FCSTD DOCUMENT  (FreeCAD 1.2R20260113 (Git shallow))
Label: Chaine verouillable
License: Creative Commons Attribution-NonCommercial-ShareAlike 4.0
LicenseURL: https://creativecommons.org/licenses/by-nc-sa/4.0/
objects: Sketcher::SketchObject×15, App::Point×12, PartDesign::Pocket×10, PartDesign::Body×9, PartDesign::SubShapeBinder×6, PartDesign::Pad×6, PartDesign::Mirrored×5, Part::FeaturePython×4, PartDesign::Draft×3, PartDesign::Chamfer×3, App::Part×3, PartDesign::FeatureBase×2, PartDesign::FeaturePython×2, PartDesign::Thickness×1, App::VarSet×1, Part::DatumLine×1, PartDesign::Hole×1, PartDesign::Groove×1
note: 142 computed .brp shape members not serialized (recipe doc carries the construction recipe); baked Part::Feature solids carry a one-line shape summary decoded from their .brp

FEATURE [App::Point] Origin001  label="Origine"
  Role = Origin
FEATURE [Sketcher::SketchObject] Sketch  label="Master"
  ArcFitTolerance = 1e-06
  AttachmentSupport = -> [Origin]
  ExternalTypes = [0]
  FullyConstrained = true
  MakeInternals = false
  MapMode = 5
  sketch-geometry (8):
    g0: ArcOfCircle CenterX=0 CenterY=1.93649 CenterZ=0 NormalX=0 NormalY=0 NormalZ=1 AngleXU=0 Radius=4 StartAngle=5.77782 EndAngle=9.93014
    g1: ArcOfCircle CenterX=7 CenterY=-1.93649 CenterZ=0 NormalX=0 NormalY=0 NormalZ=1 AngleXU=0 Radius=4 StartAngle=2.63623 EndAngle=4.71239
    g2: ArcOfCircle CenterX=-7 CenterY=-1.93649 CenterZ=0 NormalX=0 NormalY=0 NormalZ=1 AngleXU=0 Radius=4 StartAngle=4.71239 EndAngle=6.78855
    g3: LineSegment StartX=-7 StartY=-5.93649 StartZ=0 EndX=-7 EndY=-9.93649 EndZ=0
    g4: LineSegment StartX=-7 StartY=-9.93649 StartZ=0 EndX=7 EndY=-9.93649 EndZ=0
    g5: LineSegment StartX=7 StartY=-9.93649 StartZ=0 EndX=7 EndY=-5.93649 EndZ=0
    g6: LineSegment [constr] StartX=0 StartY=1.93649 StartZ=0 EndX=0 EndY=0 EndZ=0
    g7: LineSegment [constr] StartX=7 StartY=-1.93649 StartZ=0 EndX=7 EndY=0 EndZ=0
  constraints (23):
    c: Symmetric(g2,g1,g-2)
    c: Tangent(g2,g0) = 1.5708
    c: Tangent(g1,g0) = 1.5708
    c: Equal(g1,g0)
    c: Radius(g0) = 4
    c: Coincident(g2,g3)
    c: Coincident(g3,g4)
    c: Horizontal(g4)
    c: Coincident(g4,g5)
    c: Coincident(g5,g1)
    c: Vertical(g5)
    c: Vertical(g1,g1)
    c: Vertical(g2,g2)
    c: Vertical(g3)
    c: Distance(g5,g5) = 4
    c: PointOnObject(g0,g-2)
    c: Coincident(g6,g0)
    c: Coincident(g6,g-1)
    c: Coincident(g7,g1)
    c: PointOnObject(g7,g-1)
    c: Vertical(g7)
    c: Equal(g7,g6)
    c: Distance(g4,g4) = 14
FEATURE [App::Point] Origin003  label="Origine002"
  Role = Origin
FEATURE [PartDesign::SubShapeBinder] Binder
  BindCopyOnChange = 0
  BindMode = 0
  ClaimChildren = false
  Context = -> Body001 [Binder.]
  Fuse = false
  MakeFace = true
  OffsetFill = false
  OffsetIntersection = false
  OffsetJoinType = 0
  OffsetOpenResult = false
  PartialLoad = false
  Refine = true
  Relative = true
  Support = -> [Body[Sketch.]]
  _Version = 2
FEATURE [PartDesign::Pad] Pad
  Direction = (0,0,1)
  Length = 10
  Length2 = 10
  Profile = -> Binder [Face1]
  Refine = true
  SideType = 0
  Suppressed = false
  Type = 0
  Type2 = 0
FEATURE [PartDesign::Draft] Draft
  Angle = -10
  Base = -> Pad [Face6,Face1,Face2]
  BaseFeature = -> Pad
  Refine = true
  SupportTransform = false
  Suppressed = false
FEATURE [PartDesign::Mirrored] Mirrored
  BaseFeature = -> Draft
  MirrorPlane = -> XY_Plane001
  Originals = -> [Draft]
  Refine = true
  Suppressed = false
  TransformMode = 1
FEATURE [PartDesign::Body] Body001  label="v1 Male"
  AllowCompound = false
  Group = -> [Binder,Pad,Draft,Mirrored]
  Origin = -> Origin002
  Tip = -> Mirrored
FEATURE [App::Point] Origin005  label="Origine004"
  Role = Origin
FEATURE [Sketcher::SketchObject] Sketch001
  ArcFitTolerance = 1e-06
  AttachmentSupport = -> [Origin]
  ExternalGeometry = -> [Sketch]
  ExternalTypes = [0,0]
  FullyConstrained = true
  MakeInternals = false
  MapMode = 5
  sketch-geometry (6):
    g0: ArcOfCircle CenterX=7 CenterY=-1.93649 CenterZ=0 NormalX=0 NormalY=0 NormalZ=1 AngleXU=0 Radius=4 StartAngle=2.63623 EndAngle=6.78855
    g1: ArcOfCircle CenterX=0 CenterY=1.93649 CenterZ=0 NormalX=0 NormalY=0 NormalZ=1 AngleXU=0 Radius=4 StartAngle=5.77782 EndAngle=7.85398
    g2: ArcOfCircle CenterX=14 CenterY=1.93649 CenterZ=0 NormalX=0 NormalY=0 NormalZ=1 AngleXU=0 Radius=4 StartAngle=1.5708 EndAngle=3.64695
    g3: LineSegment StartX=1.2e-15 StartY=5.93649 StartZ=0 EndX=1.2e-15 EndY=7.93649 EndZ=0
    g4: LineSegment StartX=1.2e-15 StartY=7.93649 StartZ=0 EndX=14 EndY=7.93649 EndZ=0
    g5: LineSegment StartX=14 StartY=7.93649 StartZ=0 EndX=14 EndY=5.93649 EndZ=0
  constraints (18):
    c: Coincident(g0,g-3)
    c: Coincident(g0,g-4)
    c: PointOnObject(g0,g-1)
    c: Coincident(g1,g-4)
    c: Coincident(g1,g0)
    c: Coincident(g2,g0)
    c: Coincident(g1,g3)
    c: Coincident(g3,g4)
    c: Horizontal(g4)
    c: Coincident(g4,g5)
    c: Coincident(g5,g2)
    c: Vertical(g5)
    c: Equal(g2,g1)
    c: Horizontal(g2,g1)
    c: Vertical(g3)
    c: Distance(g5,g5) = 2
    c: Vertical(g2,g2)
    c: Vertical(g1,g-1)
FEATURE [PartDesign::Body] Body
  AllowCompound = false
  Group = -> [Sketch,Sketch001]
  Origin = -> Origin
FEATURE [PartDesign::SubShapeBinder] Binder001
  BindCopyOnChange = 0
  BindMode = 0
  ClaimChildren = false
  Context = -> Body002 [Binder001.]
  Fuse = false
  MakeFace = true
  OffsetFill = false
  OffsetIntersection = false
  OffsetJoinType = 0
  OffsetOpenResult = false
  PartialLoad = false
  Refine = true
  Relative = true
  Support = -> [Body[Sketch001.]]
  _Version = 2
FEATURE [PartDesign::Pad] Pad001
  Direction = (0,0,1)
  Length = 10
  Length2 = 10
  Profile = -> Binder001
  Refine = true
  SideType = 0
  Suppressed = false
  Type = 0
  Type2 = 0
FEATURE [PartDesign::Draft] Draft001
  Angle = 10
  Base = -> Pad001 [Face6,Face1,Face2]
  BaseFeature = -> Pad001
  Refine = true
  SupportTransform = false
  Suppressed = false
FEATURE [PartDesign::Thickness] Thickness
  Base = -> Draft001 [Face8]
  BaseFeature = -> Draft001
  Intersection = true
  Join = 0
  Mode = 0
  Refine = true
  Reversed = true
  SupportTransform = false
  Suppressed = false
  Value = 2
FEATURE [PartDesign::Mirrored] Mirrored001
  BaseFeature = -> Thickness
  MirrorPlane = -> XY_Plane002
  Originals = -> [Draft001]
  Refine = true
  Suppressed = false
  TransformMode = 1
FEATURE [PartDesign::Body] Body002  label="v1 Female"
  AllowCompound = false
  Group = -> [Binder001,Pad001,Draft001,Thickness,Mirrored001]
  Origin = -> Origin004
  Placement = pos=(-7,0,0) rot=(0,0,1;3.14159rad)
  Tip = -> Mirrored001
FEATURE [App::Point] Origin007  label="Origine006"
  Role = Origin
FEATURE [Sketcher::SketchObject] Sketch002
  ArcFitTolerance = 1e-06
  AttachmentSupport = -> [Origin006]
  ExternalTypes = [0]
  FullyConstrained = true
  MakeInternals = false
  MapMode = 5
  sketch-geometry (13):
    g0: LineSegment StartX=-10 StartY=10 StartZ=0 EndX=-10 EndY=-10 EndZ=0
    g1: LineSegment StartX=-10 StartY=-10 StartZ=0 EndX=-8 EndY=-10 EndZ=0
    g2: LineSegment StartX=-8 StartY=-10 StartZ=0 EndX=-8 EndY=0 EndZ=0
    g3: LineSegment StartX=-8 StartY=0 StartZ=0 EndX=8 EndY=0 EndZ=0
    g4: LineSegment StartX=8 StartY=0 StartZ=0 EndX=8 EndY=-10 EndZ=0
    g5: LineSegment StartX=8 StartY=-10 StartZ=0 EndX=10 EndY=-10 EndZ=0
    g6: LineSegment StartX=10 StartY=-10 StartZ=0 EndX=10 EndY=10 EndZ=0
    g7: LineSegment StartX=10 StartY=10 StartZ=0 EndX=8 EndY=10 EndZ=0
    g8: LineSegment StartX=8 StartY=10 StartZ=0 EndX=8 EndY=2 EndZ=0
    g9: LineSegment StartX=8 StartY=2 StartZ=0 EndX=-8 EndY=2 EndZ=0
    g10: LineSegment StartX=-8 StartY=2 StartZ=0 EndX=-8 EndY=10 EndZ=0
    g11: LineSegment StartX=-8 StartY=10 StartZ=0 EndX=-10 EndY=10 EndZ=0
    g12: LineSegment [constr] StartX=-8 StartY=2 StartZ=0 EndX=-8 EndY=0 EndZ=0
  constraints (36):
    c: Coincident(g0,g1)
    c: Coincident(g1,g2)
    c: PointOnObject(g2,g-1)
    c: Vertical(g2)
    c: Coincident(g2,g3)
    c: PointOnObject(g3,g-1)
    c: Coincident(g3,g4)
    c: Vertical(g4)
    c: Coincident(g4,g5)
    c: Horizontal(g5)
    c: Coincident(g5,g6)
    c: Vertical(g6)
    c: Coincident(g6,g7)
    c: Horizontal(g7)
    c: Coincident(g7,g8)
    c: Coincident(g8,g9)
    c: Horizontal(g9)
    c: Coincident(g9,g10)
    c: Vertical(g10)
    c: Coincident(g10,g11)
    c: Coincident(g11,g0)
    c: Horizontal(g11)
    c: Vertical(g8)
    c: Coincident(g12,g9)
    c: Coincident(g12,g2)
    c: Vertical(g12)
    c: Equal(g12,g11)
    c: Equal(g11,g7)
    c: Distance(g11,g11) = 2
    c: DistanceY(g0,g0) = 20
    c: Horizontal(g1)
    c: DistanceX(g0,g5) = 20
    c: Symmetric(g1,g4,g-2)
    c: Symmetric(g0,g0,g-1)
    c: Horizontal(g10,g7)
    c: Vertical(g3,g8)
FEATURE [PartDesign::Pad] Pad002
  Direction = (0,0,1)
  Length = 18.8496
  Length2 = 10
  Profile = -> Sketch002
  ReferenceAxis = -> Sketch002 [N_Axis]
  Refine = true
  SideType = 2
  Suppressed = false
  Type = 0
  Type2 = 0
  expr: Length = 6 * pi
FEATURE [Sketcher::SketchObject] Sketch003
  ArcFitTolerance = 1e-06
  ExternalGeometry = -> [Pad002]
  ExternalTypes = [0,0]
  FullyConstrained = true
  MakeInternals = false
  MapMode = 5
  Placement = pos=(8,0,0) rot=(0.57735,-0.57735,-0.57735;2.0944rad)
  sketch-geometry (10):
    g0: LineSegment StartX=-10 StartY=13.4248 StartZ=0 EndX=-10 EndY=4.42478 EndZ=0
    g1: LineSegment StartX=-10 StartY=4.42478 StartZ=0 EndX=-2 EndY=4.42478 EndZ=0
    g2: LineSegment StartX=-2 StartY=4.42478 StartZ=0 EndX=-2 EndY=13.4248 EndZ=0
    g3: ArcOfCircle CenterX=-6 CenterY=13.4248 CenterZ=0 NormalX=0 NormalY=0 NormalZ=1 AngleXU=0 Radius=4 StartAngle=1e-16 EndAngle=3.14159
    g4: LineSegment StartX=0 StartY=4.42478 StartZ=0 EndX=0 EndY=9.92478 EndZ=0
    g5: LineSegment StartX=10 StartY=11.4248 StartZ=0 EndX=10 EndY=4.42478 EndZ=0
    g6: LineSegment StartX=10 StartY=4.42478 StartZ=0 EndX=0 EndY=4.42478 EndZ=0
    g7: LineSegment StartX=1.5 StartY=11.4248 StartZ=0 EndX=10 EndY=11.4248 EndZ=0
    g8: ArcOfCircle CenterX=1.5 CenterY=9.92478 CenterZ=0 NormalX=0 NormalY=0 NormalZ=1 AngleXU=0 Radius=1.5 StartAngle=1.5708 EndAngle=3.14159
    g9: GeomPoint [constr] X=0 Y=11.4248 Z=0
  constraints (27):
    c: Vertical(g0)
    c: Coincident(g0,g1)
    c: Horizontal(g1)
    c: Coincident(g1,g2)
    c: Vertical(g2)
    c: Tangent(g2,g3) = -1.5708
    c: PointOnObject(g-3,g2)
    c: PointOnObject(g-3,g0)
    c: Tangent(g3,g0) = -1.5708
    c: PointOnObject(g4,g-2)
    c: PointOnObject(g9,g-2)
    c: Coincident(g5,g6)
    c: Coincident(g6,g4)
    c: Horizontal(g6)
    c: Vertical(g5)
    c: DistanceY(g-3,g5) = 2
    c: DistanceY(g0,g-3) = 5
    c: Horizontal(g4,g1)
    c: Vertical(g5,g-4)
    c: Coincident(g7,g5)
    c: Horizontal(g7)
    c: Tangent(g-3,g3)
    c: PointOnObject(g9,g4)
    c: PointOnObject(g9,g7)
    c: Tangent(g4,g8) = 1.5708
    c: Tangent(g7,g8) = 1.5708
    c: Radius(g8) = 1.5
FEATURE [PartDesign::Pad] Pad003
  BaseFeature = -> Pad002
  Direction = (-1,1e-16,-1e-16)
  Length = 2
  Length2 = 10
  Profile = -> Sketch003
  ReferenceAxis = -> Sketch003 [N_Axis]
  Refine = true
  SideType = 0
  Suppressed = false
  Type = 0
  Type2 = 0
FEATURE [Sketcher::SketchObject] Sketch004
  ArcFitTolerance = 1e-06
  ExternalGeometry = -> [Pad003]
  ExternalTypes = [0]
  FullyConstrained = true
  MakeInternals = false
  MapMode = 5
  Placement = pos=(7.85,-3.3e-15,0) rot=(0.57735,0.57735,0.57735;2.0944rad)
  sketch-geometry (1):
    g0: Circle CenterX=6 CenterY=13.4248 CenterZ=0 NormalX=0 NormalY=0 NormalZ=1 AngleXU=0 Radius=2
  constraints (2):
    c: Diameter(g0) = 4
    c: Coincident(g0,g-3)
FEATURE [Sketcher::SketchObject] Sketch006
  ArcFitTolerance = 1e-06
  AttachmentSupport = -> [YZ_Plane]
  ExternalGeometry = -> [Pad003]
  ExternalTypes = [0,0]
  FullyConstrained = true
  MakeInternals = false
  MapMode = 5
  Placement = pos=(0,0,0) rot=(0.57735,0.57735,0.57735;2.0944rad)
  sketch-geometry (7):
    g0: ArcOfCircle [constr] CenterX=6 CenterY=-6 CenterZ=0 NormalX=0 NormalY=0 NormalZ=1 AngleXU=0 Radius=4 StartAngle=4.16945 EndAngle=6.28319
    g1: ArcOfCircle CenterX=5.62019 CenterY=-5.67481 CenterZ=0 NormalX=0 NormalY=0 NormalZ=1 AngleXU=0 Radius=3.74997 StartAngle=4.71239 EndAngle=5.3245
    g2: LineSegment StartX=5.62019 StartY=-9.42478 StartZ=0 EndX=10 EndY=-9.42478 EndZ=0
    g3: LineSegment StartX=10 StartY=-9.42478 StartZ=0 EndX=10 EndY=-5.67481 EndZ=0
    g4: LineSegment [constr] StartX=10 StartY=-9.42478 StartZ=0 EndX=5.62019 EndY=-5.67481 EndZ=0
    g5: LineSegment StartX=7.7749 StartY=-8.74393 StartZ=0 EndX=9.89622 EndY=-6.62261 EndZ=0
    g6: ArcOfCircle CenterX=5.62019 CenterY=-5.67481 CenterZ=0 NormalX=0 NormalY=0 NormalZ=1 AngleXU=0 Radius=4.37981 StartAngle=6.06506 EndAngle=6.28319
  constraints (18):
    c: Coincident(g0,g-3)
    c: PointOnObject(g6,g-4)
    c: Distance(g0,g1) = 0.5
    c: Coincident(g2,g-4)
    c: Horizontal(g2)
    c: Coincident(g3,g2)
    c: Tangent(g3,g6) = -1.5708
    c: PointOnObject(g0,g2)
    c: Tangent(g0,g3) = -1.5708
    c: Coincident(g4,g2)
    c: Coincident(g4,g1)
    c: PointOnObject(g0,g4)
    c: Angle(g2,g5) = 0.785398
    c: Distance(g5,g5) = 3
    c: Coincident(g5,g1)
    c: Coincident(g1,g6)
    c: Coincident(g5,g6)
    c: Tangent(g1,g2) = -1.5708
FEATURE [App::Point] Origin009  label="Origine008"
  Role = Origin
FEATURE [PartDesign::Pocket] Pocket003
  BaseFeature = -> Pad003
  Direction = (-1,4e-16,0)
  Length = 0.15
  Length2 = 5
  Profile = -> Pad003 [Face15,Face14]
  Refine = true
  SideType = 0
  Suppressed = false
  Type = 0
  Type2 = 0
FEATURE [PartDesign::Pad] Pad004
  BaseFeature = -> Pocket003
  Direction = (1,1e-16,-1e-16)
  Length = 1
  Length2 = 10
  Profile = -> Sketch004
  ReferenceAxis = -> Sketch004 [N_Axis]
  Refine = true
  SideType = 0
  Suppressed = false
  Type = 0
  Type2 = 0
FEATURE [PartDesign::Draft] Draft002
  Angle = -30
  Base = -> Pad004 [Face24,Face19]
  BaseFeature = -> Pad004
  NeutralPlane = -> Pad004 [Face13]
  Refine = true
  SupportTransform = false
  Suppressed = false
FEATURE [Sketcher::SketchObject] Sketch005
  ArcFitTolerance = 1e-06
  AttachmentSupport = -> [YZ_Plane003]
  ExternalGeometry = -> [Pad003,Pad004]
  ExternalTypes = [0,0,0]
  FullyConstrained = true
  MakeInternals = false
  MapMode = 5
  Placement = pos=(0,0,0) rot=(0.57735,-0.57735,-0.57735;2.0944rad)
  sketch-geometry (6):
    g0: Circle [constr] CenterX=-6 CenterY=-5.42478 CenterZ=0 NormalX=0 NormalY=0 NormalZ=1 AngleXU=0 Radius=2
    g1: LineSegment [constr] StartX=-6 StartY=13.4248 StartZ=0 EndX=-6 EndY=9.42478 EndZ=0
    g2: LineSegment [constr] StartX=-6 StartY=-5.42478 StartZ=0 EndX=-6 EndY=-9.42478 EndZ=0
    g3: ArcOfCircle CenterX=-6 CenterY=-5.42478 CenterZ=0 NormalX=0 NormalY=0 NormalZ=1 AngleXU=0 Radius=2.1 StartAngle=2.0944 EndAngle=7.33038
    g4: LineSegment StartX=-7.05 StartY=-3.60612 StartZ=0 EndX=-6 EndY=-2.99991 EndZ=0
    g5: LineSegment StartX=-6 StartY=-2.99991 StartZ=0 EndX=-4.95 EndY=-3.60612 EndZ=0
  constraints (16):
    c: Vertical(g1)
    c: Vertical(g2)
    c: Vertical(g0,g1)
    c: Equal(g2,g1)
    c: PointOnObject(g1,g-4)
    c: PointOnObject(g2,g-3)
    c: Equal(g0,g-5)
    c: Coincident(g2,g3)
    c: Coincident(g1,g-5)
    c: Coincident(g2,g0)
    c: Coincident(g4,g5)
    c: Vertical(g0,g4)
    c: Angle(g5,g-1) = 0.523599
    c: Distance(g0,g3) = 0.1
    c: Tangent(g4,g3) = 1.5708
    c: Tangent(g5,g3) = 1.5708
FEATURE [Sketcher::SketchObject] Sketch007
  ArcFitTolerance = 1e-06
  AttachmentSupport = -> [Origin006]
  ExternalGeometry = -> [Pad004]
  ExternalTypes = [0,0]
  FullyConstrained = true
  MakeInternals = false
  MapMode = 5
  Placement = pos=(0,0,0) rot=(1,0,0;1.5708rad)
  sketch-geometry (3):
    g0: LineSegment StartX=8 StartY=15.4248 StartZ=0 EndX=8.85 EndY=11.4248 EndZ=0
    g1: LineSegment StartX=8.85 StartY=11.4248 StartZ=0 EndX=8.85 EndY=15.4248 EndZ=0
    g2: LineSegment StartX=8.85 StartY=15.4248 StartZ=0 EndX=8 EndY=15.4248 EndZ=0
  constraints (7):
    c: Coincident(g0,g1)
    c: Coincident(g1,g2)
    c: Coincident(g2,g0)
    c: Horizontal(g2)
    c: PointOnObject(g0,g-4)
    c: Coincident(g1,g-3)
    c: Coincident(g0,g-3)
FEATURE [PartDesign::Pocket] Pocket002
  BaseFeature = -> Draft002
  Direction = (0,1,-2e-16)
  Length = 5
  Length2 = 5
  Profile = -> Sketch007
  ReferenceAxis = -> Sketch007 [N_Axis]
  Refine = true
  SideType = 2
  Suppressed = false
  Type = 1
  Type2 = 0
FEATURE [PartDesign::Pocket] Pocket001
  BaseFeature = -> Pocket002
  Direction = (-1,0,0)
  Length = 5
  Length2 = 5
  Profile = -> Sketch006
  ReferenceAxis = -> Sketch006 [N_Axis]
  Refine = true
  Reversed = true
  SideType = 0
  Suppressed = false
  Type = 1
  Type2 = 0
FEATURE [PartDesign::Mirrored] Mirrored002
  BaseFeature = -> Pocket001
  MirrorPlane = -> YZ_Plane003
  Originals = -> [Pad003,Pocket003,Pad004,Draft002,Pocket002,Pocket001]
  Refine = true
  Suppressed = false
  TransformMode = 0
FEATURE [PartDesign::Pocket] Pocket
  BaseFeature = -> Mirrored002
  Direction = (1,0,0)
  Length = 5
  Length2 = 5
  Offset = 1.2
  Profile = -> Sketch005
  ReferenceAxis = -> Sketch005 [N_Axis]
  Refine = true
  SideType = 2
  Suppressed = false
  Type = 2
  Type2 = 0
FEATURE [PartDesign::Chamfer] Chamfer
  Angle = 45
  Base = -> Pocket [Edge96,Edge92]
  BaseFeature = -> Pocket
  ChamferType = 0
  FlipDirection = false
  Refine = true
  Size = 0.7
  Size2 = 1
  SupportTransform = false
  Suppressed = false
  UseAllEdges = false
FEATURE [Part::FeaturePython] InvoluteRack  # WARN: FeaturePython — macro-defined, semantics opaque (R4)
  AttacherType = Attacher::AttachEngine3D
  Placement = pos=(-5e-16,-7.5,-10) rot=(0.57735,0.57735,0.57735;2.0944rad)
  add_endings = true
  clearance = 0.25
  double_helix = true
  head = 0
  head_fillet = 0.2
  height = 2
  helix_angle = 0
  module = 1
  num_teeth = 10
  pressure_angle = 20
  properties_from_tool = false
  root_fillet = 0.2
  simplified = false
  thickness = 10
  transverse_pitch = 3.14159
  version = 1.3.0
FEATURE [Part::FeaturePython] TimingGear  label="TimingGear004"  # WARN: FeaturePython — macro-defined, semantics opaque (R4)
  AttacherType = Attacher::AttachEngine3D
  Placement = pos=(0,-12.871,0) rot=(0,1,0;1.5708rad)
  h = 0.75
  height = 5
  num_teeth = 40
  offset = 0.4
  pitch = 2
  r0 = 0.555
  r1 = 1
  rs = 0.15
  type = 0
  u = 0.254
  version = 1.3.0
FEATURE [Part::FeaturePython] InvoluteGear  # WARN: FeaturePython — macro-defined, semantics opaque (R4)
  AttacherType = Attacher::AttachEngine3D
  Placement = pos=(-4e-16,-15.476,1.67) rot=(0,1,0;1.5708rad)
  addendum_diameter = 27.5
  angular_backlash = 0
  axle_hole = false
  axle_holesize = 10
  backlash = 0
  clearance = 0.25
  double_helix = false
  head = 0
  head_fillet = 0
  height = 5
  helix_angle = 0
  module = 1.25
  num_teeth = 20
  numpoints = 20
  offset_hole = false
  offset_holeoffset = 10
  offset_holesize = 10
  pitch_diameter = 25
  pressure_angle = 20
  properties_from_tool = false
  reversed_backlash = false
  root_diameter = 21.875
  root_fillet = 0
  shift = 0
  simple = false
  transverse_pitch = 3.92699
  traverse_module = 1.25
  undercut = false
  version = 1.3.0
  expr: angular_backlash = backlash / pitch_diameter * 360 ° / pi
FEATURE [PartDesign::SubShapeBinder] Binder003
  BindCopyOnChange = 0
  BindMode = 0
  ClaimChildren = false
  Context = -> Body003 [Binder003.]
  Fuse = false
  MakeFace = true
  OffsetFill = false
  OffsetIntersection = false
  OffsetJoinType = 0
  OffsetOpenResult = false
  PartialLoad = false
  Refine = true
  Relative = true
  Support = -> [InvoluteRack[Face85]]
  _Version = 2
FEATURE [PartDesign::Pocket] Pocket004
  BaseFeature = -> Chamfer
  Direction = (1,0,0)
  Length = 5
  Length2 = 5
  Profile = -> Binder003
  Refine = true
  SideType = 2
  Suppressed = false
  Type = 1
  Type2 = 0
FEATURE [PartDesign::Body] Body003  label="v2"
  AllowCompound = false
  Group = -> [Sketch002,Pad002,Sketch003,Pad003,Pocket003,Sketch004,Pad004,Draft002,Pocket002,Pocket001,Mirrored002,Pocket,Sketch005,Sketch006,Sketch007,Chamfer,Binder003,Pocket004]
  Origin = -> Origin006
  Tip = -> Pocket004
FEATURE [PartDesign::FeatureBase] Clone
  BaseFeature = -> Body003
  Suppressed = false
FEATURE [PartDesign::Body] Body004  label="v2 clone"
  AllowCompound = false
  Group = -> [Clone]
  Origin = -> Origin008
  Placement = pos=(0,0,-18.859) rot=(0,0,1;0rad)
  Tip = -> Clone
FEATURE [App::Part] Part  label="v1 (zipper style)"
  Group = -> [Body,Body001,Body002]
  Origin = -> Origin010
FEATURE [App::Point] Origin011  label="Origine010"
  Role = Origin
FEATURE [App::Part] Part001  label="v2 (one chain)"
  Group = -> [Body003,Body004,InvoluteRack,TimingGear,InvoluteGear]
  Origin = -> Origin012
FEATURE [App::Point] Origin013  label="Origine012"
  Role = Origin
FEATURE [App::Point] Origin015  label="Origine014"
  Role = Origin
FEATURE [App::Point] Origin017  label="Origine016"
  Role = Origin
FEATURE [Sketcher::SketchObject] Sketch008
  ArcFitTolerance = 1e-06
  AttachmentSupport = -> [Origin016]
  ExternalTypes = [0]
  FullyConstrained = true
  MakeInternals = false
  MapMode = 5
  Placement = pos=(0,0,0) rot=(0.57735,0.57735,0.57735;2.0944rad)
  expr: .Constraints.D_Primitif = <<VarSet>>.Dp1
  sketch-geometry (1):
    g0: Circle [constr] CenterX=0 CenterY=0 CenterZ=0 NormalX=0 NormalY=0 NormalZ=1 AngleXU=0 Radius=25.4648
  constraints (2):
    c: Coincident(g0,g-1)
    c: Diameter(g0) = 50.9296  'D_Primitif'
FEATURE [App::VarSet] VarSet
  Dp1 = 50.9296
  m2 = 2.03718
  z1 = 80
  z2 = 25
  expr: Dp1 = 2 * z1 / pi
  expr: m2 = 2 * z1 / (pi * z2)
FEATURE [Part::DatumLine] DatumLine  label="Axis"
  AttacherType = Attacher::AttachEngineLine
  MapMode = 42
  Placement = pos=(0,-1e-16,-1e-16) rot=(0.57735,0.57735,0.57735;2.0944rad)
FEATURE [PartDesign::FeaturePython] TimingGear001  label="TimingGear006"  # WARN: FeaturePython — macro-defined, semantics opaque (R4)
  AttacherType = Attacher::AttachEngine3D
  AttachmentSupport = -> [DatumLine]
  MapMode = 2
  Placement = pos=(0,-1e-16,-1e-16) rot=(0.57735,0.57735,0.57735;2.0944rad)
  Suppressed = false
  h = 0.75
  height = 7
  num_teeth = 80
  offset = 0.4
  pitch = 2
  r0 = 0.555
  r1 = 1
  rs = 0.15
  type = 0
  u = 0.254
  version = 1.3.0
  expr: num_teeth = <<VarSet>>.z1
FEATURE [App::Point] Origin019  label="Origine018"
  Role = Origin
FEATURE [Sketcher::SketchObject] Sketch013
  ArcFitTolerance = 1e-06
  AttachmentSupport = -> [Origin018]
  ExternalTypes = [0]
  FullyConstrained = true
  MakeInternals = false
  MapMode = 5
  Placement = pos=(0,0,0) rot=(0.57735,0.57735,0.57735;2.0944rad)
  sketch-geometry (7):
    g0: LineSegment StartX=8 StartY=0 StartZ=0 EndX=4 EndY=6.9282 EndZ=0
    g1: LineSegment StartX=4 StartY=6.9282 StartZ=0 EndX=-4 EndY=6.9282 EndZ=0
    g2: LineSegment StartX=-4 StartY=6.9282 StartZ=0 EndX=-8 EndY=9e-16 EndZ=0
    g3: LineSegment StartX=-8 StartY=9e-16 StartZ=0 EndX=-4 EndY=-6.9282 EndZ=0
    g4: LineSegment StartX=-4 StartY=-6.9282 StartZ=0 EndX=4 EndY=-6.9282 EndZ=0
    g5: LineSegment StartX=4 StartY=-6.9282 StartZ=0 EndX=8 EndY=0 EndZ=0
    g6: Circle [constr] CenterX=0 CenterY=0 CenterZ=0 NormalX=0 NormalY=0 NormalZ=1 AngleXU=0 Radius=8
  constraints (16):
    c: Coincident(g0,g1)
    c: Coincident(g1,g2)
    c: Coincident(g2,g3)
    c: Coincident(g3,g4)
    c: Coincident(g4,g5)
    c: Coincident(g5,g0)
    c: Equal(g0, g1-g5) x5
    c: PointOnObject(g0,g6)
    c: PointOnObject(g1,g6)
    c: PointOnObject(g2,g6)
    c: PointOnObject(g3,g6)
    c: PointOnObject(g4,g6)
    c: PointOnObject(g5,g6)
    c: Radius(g6) = 8
    c: Coincident(g6,g-1)
    c: PointOnObject(g5,g-1)
FEATURE [PartDesign::Pad] Pad006
  Direction = (1,0,0)
  Length = 30
  Length2 = 10
  Profile = -> Sketch013
  ReferenceAxis = -> Sketch013 [N_Axis]
  Refine = true
  SideType = 2
  Suppressed = false
  Type = 0
  Type2 = 0
FEATURE [Sketcher::SketchObject] Sketch014
  ArcFitTolerance = 1e-06
  AttachmentSupport = -> [Pad006]
  ExternalGeometry = -> [Pad006]
  ExternalTypes = [0]
  FullyConstrained = true
  MakeInternals = false
  MapMode = 5
  Placement = pos=(15,0,0) rot=(0.57735,0.57735,0.57735;2.0944rad)
  sketch-geometry (1):
    g0: Circle CenterX=0 CenterY=0 CenterZ=0 NormalX=0 NormalY=0 NormalZ=1 AngleXU=0 Radius=5.7282
  constraints (2):
    c: Coincident(g0,g-1)
    c: Distance(g0,g-3) = 1.2
FEATURE [Part::FeaturePython] ScrewTap001  label="M10x40-Taraud à vis"  # WARN: FeaturePython — macro-defined, semantics opaque (R4)
  BaseObject = -> Part002 [Body006.Mirrored003.Edge45]
  Diameter = 10
  DiameterCustom = 8
  Invert = true
  LeftHanded = false
  Length = 40
  MatchOuter = true
  Offset = 10
  OffsetAngle = 0
  PitchCustom = 2
  Placement = pos=(-22,4.9e-15,-4.9e-15) rot=(0,-1,0;1.5708rad)
  Thread = true
  Type = 2
FEATURE [App::Point] Origin021  label="Origine020"
  Role = Origin
FEATURE [Sketcher::SketchObject] Sketch018  label="Hole Footprint"
  ArcFitTolerance = 1e-06
  AttachmentSupport = -> [Origin018]
  ExternalTypes = [0,0,0,0,0,0]
  FullyConstrained = false
  MakeInternals = false
  MapMode = 5
  Placement = pos=(0,0,0) rot=(0.57735,0.57735,0.57735;2.0944rad)
  sketch-geometry (12):
    g0: LineSegment StartX=8.11547 StartY=-1.1e-15 StartZ=0 EndX=4.05774 EndY=7.0282 EndZ=0
    g1: LineSegment StartX=4.05774 StartY=7.0282 StartZ=0 EndX=-4.05774 EndY=7.0282 EndZ=0
    g2: LineSegment StartX=-4.05774 StartY=7.0282 StartZ=0 EndX=-8.11547 EndY=2.7e-15 EndZ=0
    g3: LineSegment StartX=-8.11547 StartY=2.7e-15 StartZ=0 EndX=-4.05774 EndY=-7.0282 EndZ=0
    g4: LineSegment StartX=-4.05774 StartY=-7.0282 StartZ=0 EndX=4.05774 EndY=-7.0282 EndZ=0
    g5: LineSegment StartX=4.05774 StartY=-7.0282 StartZ=0 EndX=8.11547 EndY=-9e-16 EndZ=0
    g6: LineSegment [constr] StartX=8.11716 StartY=-0.00292065 StartZ=0 EndX=8.03055 EndY=-0.0529206 EndZ=0
    g7: LineSegment [constr] StartX=4.11547 StartY=7.0282 StartZ=0 EndX=4.11547 EndY=6.9282 EndZ=0
    g8: LineSegment [constr] StartX=-4.00003 StartY=7.12815 StartZ=0 EndX=-3.91343 EndY=7.07815 EndZ=0
    g9: LineSegment [constr] StartX=-8.1155 StartY=5.08068e-05 StartZ=0 EndX=-8.0289 EndY=0.0500508 EndZ=0
    g10: LineSegment [constr] StartX=-4.11547 StartY=-7.0282 StartZ=0 EndX=-4.11547 EndY=-6.9282 EndZ=0
    g11: LineSegment [constr] StartX=4.00003 StartY=-7.12815 StartZ=0 EndX=3.91343 EndY=-7.07815 EndZ=0
  constraints (36):
    c: Coincident(g0,g1)
    c: Coincident(g0,g5)
    c: Coincident(g1,g2)
    c: Coincident(g2,g3)
    c: Coincident(g3,g4)
    c: Coincident(g4,g5)
    c: Perpendicular(g6,g0)
    c: PointOnObject(g6,g0)
    c: PointOnObject(g6,g-8)
    c: Perpendicular(g7,g1)
    c: PointOnObject(g7,g1)
    c: PointOnObject(g7,g-3)
    c: Perpendicular(g8,g2)
    c: PointOnObject(g8,g2)
    c: PointOnObject(g8,g-4)
    c: Perpendicular(g9,g3)
    c: PointOnObject(g9,g3)
    c: PointOnObject(g9,g-5)
    c: Perpendicular(g10,g4)
    c: PointOnObject(g10,g4)
    c: PointOnObject(g10,g-6)
    c: Perpendicular(g11,g5)
    c: PointOnObject(g11,g5)
    c: PointOnObject(g11,g-7)
    c: Parallel(g5,g-7)
    c: Parallel(g0,g-8)
    c: Parallel(g1,g-3)
    c: Equal(g7,g6)
    c: Parallel(g2,g-4)
    c: Equal(g8,g6)
    c: Parallel(g3,g-5)
    c: Equal(g9,g6)
    c: Parallel(g4,g-6)
    c: Equal(g10,g6)
    c: Equal(g11,g6)
    c: Distance(g6) = 0.1
FEATURE [PartDesign::SubShapeBinder] Binder005
  BindCopyOnChange = 0
  BindMode = 0
  ClaimChildren = false
  Context = -> Part002 [Body007.Binder005.]
  Fuse = false
  MakeFace = true
  OffsetFill = false
  OffsetIntersection = false
  OffsetJoinType = 0
  OffsetOpenResult = false
  PartialLoad = false
  Refine = true
  Relative = true
  Support = -> [Body006[Sketch018.]]
  _Version = 2
FEATURE [PartDesign::FeaturePython] InvoluteGear002  label="InvoluteGear003"  # WARN: FeaturePython — macro-defined, semantics opaque (R4)
  AttacherType = Attacher::AttachEngine3D
  AttachmentSupport = -> [Origin020]
  MapMode = 7
  Placement = pos=(0,0,0) rot=(0.57735,-0.57735,-0.57735;2.0944rad)
  Suppressed = false
  addendum_diameter = 56.8005
  angular_backlash = 0
  axle_hole = false
  axle_holesize = 10
  backlash = 0
  clearance = 0.25
  double_helix = false
  head = 0
  head_fillet = 0.2
  height = 6
  helix_angle = 15
  module = 2.03718
  num_teeth = 25
  numpoints = 20
  offset_hole = false
  offset_holeoffset = 10
  offset_holesize = 10
  pitch_diameter = 52.7262
  pressure_angle = 20
  properties_from_tool = true
  reversed_backlash = false
  root_diameter = 47.6332
  root_fillet = 0.2
  shift = 0
  simple = false
  transverse_pitch = 6.62577
  traverse_module = 2.10905
  undercut = true
  version = 1.3.0
  expr: angular_backlash = backlash / pitch_diameter * 360 ° / pi
  expr: module = <<VarSet>>.m2
  expr: num_teeth = <<VarSet>>.z2
FEATURE [PartDesign::Pocket] Pocket008
  BaseFeature = -> InvoluteGear002
  Direction = (-1,0,0)
  Length = 5
  Length2 = 5
  Placement = pos=(0,0,0) rot=(0.57735,-0.57735,-0.57735;2.0944rad)
  Profile = -> Binder005
  Refine = true
  SideType = 2
  Suppressed = false
  Type = 1
  Type2 = 0
FEATURE [PartDesign::Chamfer] Chamfer001
  Angle = 45
  Base = -> Pocket008 [Edge411,Edge416,Edge415,Edge414,Edge413,Edge412,Edge206,Edge207,Edge208,Edge209,Edge210,Edge211]
  BaseFeature = -> Pocket008
  ChamferType = 0
  FlipDirection = false
  Placement = pos=(0,0,0) rot=(0.57735,-0.57735,-0.57735;2.0944rad)
  Refine = true
  Size = 0.5
  Size2 = 1
  SupportTransform = false
  Suppressed = false
  UseAllEdges = false
FEATURE [PartDesign::Body] Body007  label="Gear1"
  AllowCompound = true
  Group = -> [Binder005,InvoluteGear002,Pocket008,Chamfer001]
  Origin = -> Origin020
  Placement = pos=(-3.5,0,0) rot=(0,0,1;0rad)
  Tip = -> Chamfer001
FEATURE [App::Point] Origin023  label="Origine022"
  Role = Origin
FEATURE [PartDesign::SubShapeBinder] Binder006
  BindCopyOnChange = 0
  BindMode = 0
  ClaimChildren = false
  Context = -> Part002 [Body008.Binder006.]
  Fuse = false
  MakeFace = true
  OffsetFill = false
  OffsetIntersection = false
  OffsetJoinType = 0
  OffsetOpenResult = false
  PartialLoad = false
  Refine = true
  Relative = true
  Support = -> [Body007]
  _Version = 2
FEATURE [PartDesign::FeatureBase] BaseFeature
  BaseFeature = -> Binder006
  Suppressed = false
FEATURE [PartDesign::Mirrored] Mirrored004
  BaseFeature = -> BaseFeature
  MirrorPlane = -> YZ_Plane011
  Refine = true
  Suppressed = false
  TransformMode = 1
FEATURE [Sketcher::SketchObject] Sketch019
  ArcFitTolerance = 1e-06
  AttachmentSupport = -> [Origin022]
  ExternalTypes = [0]
  FullyConstrained = true
  MakeInternals = false
  MapMode = 5
  sketch-geometry (4):
    g0: LineSegment StartX=-20 StartY=40 StartZ=0 EndX=-20 EndY=-40 EndZ=0
    g1: LineSegment StartX=-20 StartY=-40 StartZ=0 EndX=0 EndY=-40 EndZ=0
    g2: LineSegment StartX=0 StartY=-40 StartZ=0 EndX=0 EndY=40 EndZ=0
    g3: LineSegment StartX=0 StartY=40 StartZ=0 EndX=-20 EndY=40 EndZ=0
  constraints (11):
    c: Coincident(g0,g1)
    c: Coincident(g1,g2)
    c: Coincident(g2,g3)
    c: Coincident(g3,g0)
    c: Vertical(g2)
    c: Horizontal(g1)
    c: Horizontal(g3)
    c: PointOnObject(g1,g-2)
    c: Symmetric(g0,g0,g-1)
    c: DistanceY(g0,g0) = 80
    c: Distance(g1,g1) = 20
FEATURE [PartDesign::Pocket] Pocket009
  BaseFeature = -> Mirrored004
  Direction = (0,0,-1)
  Length = 5
  Length2 = 5
  Profile = -> Sketch019
  ReferenceAxis = -> Sketch019 [N_Axis]
  Refine = true
  SideType = 2
  Suppressed = false
  Type = 1
  Type2 = 0
FEATURE [PartDesign::Body] Body008  label="Gear2"
  AllowCompound = true
  BaseFeature = -> Binder006
  Group = -> [BaseFeature,Binder006,Mirrored004,Sketch019,Pocket009]
  Origin = -> Origin022
  Tip = -> Pocket009
FEATURE [PartDesign::SubShapeBinder] Binder007
  BindCopyOnChange = 0
  BindMode = 0
  ClaimChildren = false
  Context = -> Part002 [Body005.Binder007.]
  Fuse = false
  MakeFace = true
  OffsetFill = false
  OffsetIntersection = false
  OffsetJoinType = 0
  OffsetOpenResult = false
  PartialLoad = false
  Refine = true
  Relative = true
  Support = -> [Body006[Sketch018.]]
  _Version = 2
FEATURE [PartDesign::Pocket] Pocket010
  BaseFeature = -> TimingGear001
  Direction = (-1,0,0)
  Length = 5
  Length2 = 5
  Placement = pos=(0,-1e-16,-1e-16) rot=(0.57735,0.57735,0.57735;2.0944rad)
  Profile = -> Binder007
  Refine = true
  SideType = 2
  Suppressed = false
  Type = 1
  Type2 = 0
FEATURE [PartDesign::Chamfer] Chamfer002
  Angle = 45
  Base = -> Pad006 [Face7,Face8]
  BaseFeature = -> Pad006
  ChamferType = 0
  FlipDirection = false
  Refine = true
  Size = 0.7
  Size2 = 1
  SupportTransform = false
  Suppressed = false
  UseAllEdges = false
FEATURE [PartDesign::Pocket] Pocket005
  BaseFeature = -> Chamfer002
  Direction = (-1,0,0)
  Length = 3
  Length2 = 5
  Profile = -> Sketch014
  ReferenceAxis = -> Sketch014 [N_Axis]
  Refine = true
  SideType = 0
  Suppressed = false
  Type = 0
  Type2 = 0
FEATURE [PartDesign::Mirrored] Mirrored003
  BaseFeature = -> Pocket005
  MirrorPlane = -> YZ_Plane009
  Originals = -> [Pocket005]
  Refine = true
  Suppressed = false
  TransformMode = 0
FEATURE [PartDesign::Hole] Hole
  BaseFeature = -> Mirrored003
  BaseProfileType = 7
  CustomThreadClearance = 0
  Depth = 74.1645
  DepthType = 1
  Diameter = 6.828
  DrillForDepth = false
  DrillPoint = 1
  DrillPointAngle = 118
  HoleCutCountersinkAngle = 90
  HoleCutCustomValues = false
  HoleCutDepth = 0
  HoleCutDiameter = 0
  HoleCutType = 0
  ModelThread = true
  Profile = -> Mirrored003 [Face23]
  Refine = true
  Suppressed = false
  Tapered = false
  TaperedAngle = 90
  ThreadClass = 0
  ThreadDepth = 74.1645
  ThreadDepthType = 0
  ThreadDiameter = 8
  ThreadDirection = 0
  ThreadFit = 0
  ThreadSize = 16
  ThreadType = 1
  Threaded = true
  UseCustomThreadClearance = false
FEATURE [Sketcher::SketchObject] Sketch015
  ArcFitTolerance = 1e-06
  AttachmentSupport = -> [Origin018]
  ExternalGeometry = -> [Hole]
  ExternalTypes = [0,0]
  FullyConstrained = true
  MakeInternals = false
  MapMode = 5
  Placement = pos=(0,0,0) rot=(0.57735,0.57735,0.57735;2.0944rad)
  sketch-geometry (3):
    g0: LineSegment StartX=-1.44283 StartY=3.09413 StartZ=0 EndX=0 EndY=3.76693 EndZ=0
    g1: LineSegment StartX=0 StartY=3.76693 StartZ=0 EndX=1.44282 EndY=3.09413 EndZ=0
    g2: LineSegment StartX=1.44282 StartY=3.09413 StartZ=0 EndX=-1.44283 EndY=3.09413 EndZ=0
  constraints (8):
    c: Coincident(g0,g1)
    c: Coincident(g1,g2)
    c: Coincident(g2,g0)
    c: Horizontal(g2)
    c: Angle(g-1,g0) = 0.436332
    c: PointOnObject(g1,g-3)
    c: Tangent(g0,g-3) = 1.5708
    c: PointOnObject(g0,g-2)
FEATURE [PartDesign::Pocket] Pocket006
  BaseFeature = -> Hole
  Direction = (-1,0,0)
  Length = 5
  Length2 = 5
  Profile = -> Sketch015
  ReferenceAxis = -> Sketch015 [N_Axis]
  Refine = true
  SideType = 2
  Suppressed = false
  Type = 1
  Type2 = 0
FEATURE [PartDesign::Body] Body006  label="Axis001"
  AllowCompound = true
  Group = -> [Sketch013,Pad006,Chamfer002,Sketch014,Pocket005,Mirrored003,Hole,Sketch015,Pocket006,Sketch018]
  Origin = -> Origin018
  Tip = -> Pocket006
FEATURE [Sketcher::SketchObject] Sketch021
  ArcFitTolerance = 1e-06
  AttachmentSupport = -> [Origin016]
  ExternalGeometry = -> [Pocket010]
  ExternalTypes = [0]
  FullyConstrained = true
  MakeInternals = false
  MapMode = 5
  sketch-geometry (8):
    g0: Circle [constr] CenterX=7 CenterY=25.1998 CenterZ=0 NormalX=0 NormalY=0 NormalZ=1 AngleXU=0 Radius=0.5
    g1: LineSegment StartX=7.5 StartY=25.6998 StartZ=0 EndX=5.79289 EndY=25.6998 EndZ=0
    g2: LineSegment StartX=5.79289 StartY=25.6998 StartZ=0 EndX=7.5 EndY=23.9927 EndZ=0
    g3: LineSegment StartX=7.5 StartY=23.9927 StartZ=0 EndX=7.5 EndY=25.6998 EndZ=0
    g4: LineSegment StartX=-0.5 StartY=25.6998 StartZ=0 EndX=1.20711 EndY=25.6998 EndZ=0
    g5: LineSegment StartX=1.20711 StartY=25.6998 StartZ=0 EndX=-0.5 EndY=23.9927 EndZ=0
    g6: LineSegment StartX=-0.5 StartY=23.9927 StartZ=0 EndX=-0.5 EndY=25.6998 EndZ=0
    g7: Circle [constr] CenterX=0 CenterY=25.1998 CenterZ=0 NormalX=0 NormalY=0 NormalZ=1 AngleXU=0 Radius=0.5
  constraints (23):
    c: Diameter(g0) = 1
    c: Coincident(g0,g-3)
    c: Horizontal(g1)
    c: Tangent(g1,g0)
    c: Coincident(g1,g2)
    c: Tangent(g2,g0)
    c: Coincident(g2,g3)
    c: Coincident(g3,g1)
    c: Tangent(g3,g0)
    c: Vertical(g3)
    c: Equal(g1,g3)
    c: Horizontal(g4)
    c: Coincident(g4,g5)
    c: Coincident(g5,g6)
    c: Coincident(g6,g4)
    c: Vertical(g6)
    c: PointOnObject(g7,g-2)
    c: Horizontal(g0,g7)
    c: Equal(g7,g0)
    c: Tangent(g4,g7)
    c: Tangent(g6,g7)
    c: Tangent(g5,g7)
    c: Equal(g6,g4)
FEATURE [PartDesign::Groove] Groove
  Angle = 360
  Angle2 = 0
  Axis = (1,0,0)
  Base = (0,0,0)
  BaseFeature = -> Pocket010
  Placement = pos=(0,-1e-16,-1e-16) rot=(0.57735,0.57735,0.57735;2.0944rad)
  Profile = -> Sketch021
  ReferenceAxis = -> X_Axis008
  Refine = true
  Reversed = true
  Suppressed = false
  Type = 0
FEATURE [PartDesign::Body] Body005  label="Timing Gear"
  AllowCompound = true
  Group = -> [Sketch008,TimingGear001,DatumLine,Binder007,Pocket010,Sketch021,Groove]
  Origin = -> Origin016
  Placement = pos=(-3.5,0,0) rot=(0,0,1;0rad)
  Tip = -> Groove
FEATURE [App::Part] Part002  label="v3 (one chain)"
  Group = -> [Body005,Body006,Body007,VarSet,Body008]
  Origin = -> Origin014
